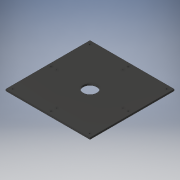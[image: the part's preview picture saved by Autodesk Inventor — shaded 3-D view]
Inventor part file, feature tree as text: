
AUTODESK INVENTOR PART (.ipt)
format: ipt  version: 2019 (Build 230136000, 136)  size: 130,560 bytes
history: native  units: mm
features: sketch x4, projected_geometry x3, extrude x2, hole x2
ambient origin geometry x8: Origin, YZ Plane, XZ Plane, XY Plane, X Axis, Y Axis, Z Axis, Center Point
bodies: Solid1 (feature_tree)
feature tree (11):
  extrude  "Extrusion1"  Depth=6.35mm TaperAngle=0.0deg
  hole  "Hole2"  [1 undecoded]
  hole  "Hole1"  [1 undecoded]
  sketch  "Sketch3"  dims[d11=4.978mm d12=12.7mm d13=11.113mm d14=6.35mm d15=14.3117mm d16=19.05mm d17=20.594885mm d18=50.0mm]
  extrude  "Extrusion3"  Depth=279.4mm
  sketch  "Sketch1"  dims[d0=304.8mm d1=6.35mm d2=0.0mm]
  sketch  "Sketch2"  dims[d3=240.513mm]
  projected_geometry  "Projected Loop1"
  projected_geometry  "Projected Loop2"
  sketch  "Sketch4"  dims[d19=3.175mm d20=0.0mm d21=279.4mm d22=279.4mm d23=6.528mm d24=12.7mm d25=11.113mm d26=3.25mm d27=14.3117mm d28=19.05mm d29=20.594885mm]
  projected_geometry  "Projected Loop3"
note: 2 required parameter values undecoded (feature->parameter linkage not recoverable at this tier; creation-order binding heuristic only, values carry confidence <= 0.55)
